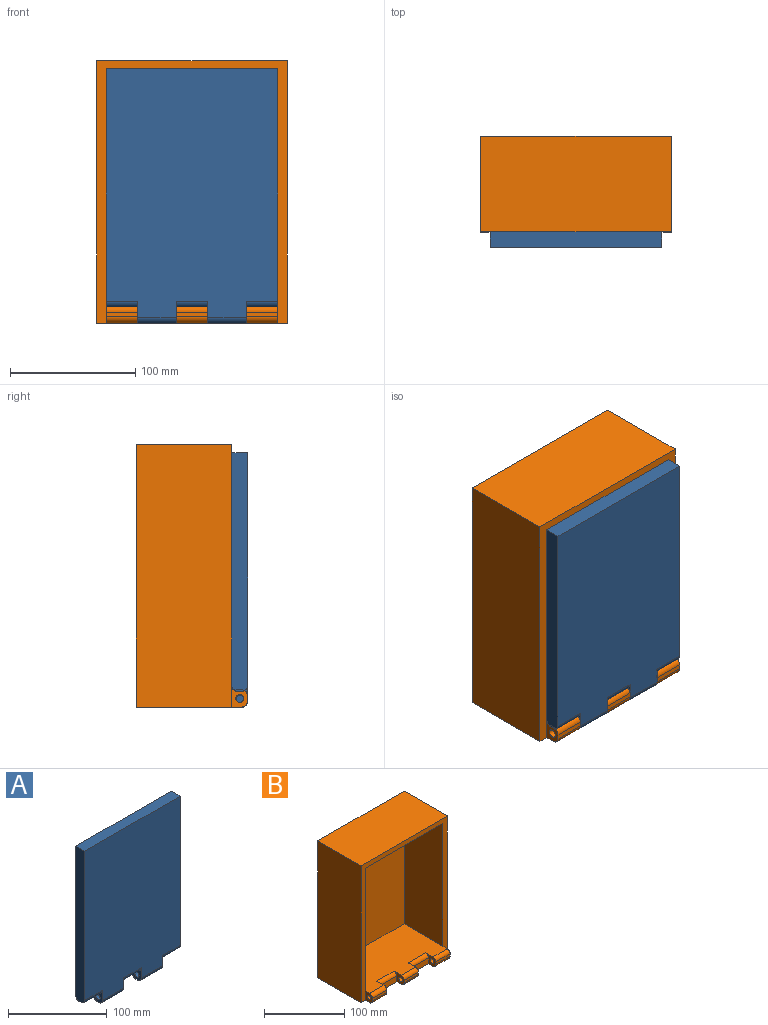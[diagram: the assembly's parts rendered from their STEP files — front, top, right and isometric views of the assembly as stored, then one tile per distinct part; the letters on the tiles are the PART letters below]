
ASSEMBLY  parts=2 mates=1
PART A: 27 faces, bbox 137.2x12.7x203.2 mm
  f0: plane 25.4x2.54mm, normal (0,0,-1), area 64.5mm2, adj f9,f11,f19,f20
  f1: plane 25.4x2.54mm, normal (0,0,-1), area 64.5mm2, adj f3,f8,f25,f26
  f2: plane 137.16x12.7mm, normal (0,0,1), area 1741.9mm2, adj f3,f5,f6,f7
  f3: plane 190.5x12.7mm, normal (-1,0,0), area 2408.3mm2, adj f1,f2,f6,f7,f25,f26
  f4: plane 25.4x2.54mm, normal (0,0,-1), area 64.5mm2, adj f5,f12,f17,f18
  f5: plane 190.5x12.7mm, normal (1,0,0), area 2408.3mm2, adj f2,f4,f6,f7,f17,f18
  f6: plane 198.12x137.16mm, normal (0,-1,0), area 26206.4mm2, adj f2,f3,f5,f8,f9,f11,f12,f17
  f7: plane 198.12x137.16mm, normal (0,1,0), area 26206.4mm2, adj f2,f3,f5,f8,f9,f11,f12,f18
  f8: plane 17.78x12.7mm, normal (-1,0,0), area 129.6mm2, adj f1,f6,f7,f10,f16,f23,f24,f25
  f9: plane 17.78x12.7mm, normal (1,0,0), area 129.6mm2, adj f0,f6,f7,f10,f16,f19,f20,f23
  f10: plane 30.48x2.54mm, normal (0,0,-1), area 77.4mm2, adj f8,f9,f23,f24
  f11: plane 17.78x12.7mm, normal (-1,0,0), area 129.6mm2, adj f0,f6,f7,f13,f15,f19,f20,f21
  f12: plane 17.78x12.7mm, normal (1,0,0), area 161.3mm2, adj f4,f6,f7,f13,f17,f18,f21,f22
  f13: plane 30.48x2.54mm, normal (0,0,-1), area 77.4mm2, adj f11,f12,f21,f22
  f14: plane 6.35x6.35mm, normal (-1,0,0), area 31.7mm2, adj f15
  f15: cylinder r=3.17mm len=20.32mm, axis (-1,0,0), area 405.4mm2, adj f11,f14
  f16: cylinder r=3.17mm len=30.48mm, axis (-1,0,0), area 608mm2, adj f8,f9
  f17: cylinder r=5.08mm len=25.4mm, axis (-1,0,0), area 202.7mm2, adj f4,f5,f6,f12
  f18: cylinder r=5.08mm len=25.4mm, axis (1,0,0), area 202.7mm2, adj f4,f5,f7,f12
  f19: cylinder r=5.08mm len=25.4mm, axis (-1,0,0), area 202.7mm2, adj f0,f6,f9,f11
  f20: cylinder r=5.08mm len=25.4mm, axis (1,0,0), area 202.7mm2, adj f0,f7,f9,f11
  f21: cylinder r=5.08mm len=30.48mm, axis (-1,0,0), area 243.2mm2, adj f7,f11,f12,f13
  f22: cylinder r=5.08mm len=30.48mm, axis (1,0,0), area 243.2mm2, adj f6,f11,f12,f13
  f23: cylinder r=5.08mm len=30.48mm, axis (-1,0,0), area 243.2mm2, adj f7,f8,f9,f10
  f24: cylinder r=5.08mm len=30.48mm, axis (1,0,0), area 243.2mm2, adj f6,f8,f9,f10
  f25: cylinder r=5.08mm len=25.4mm, axis (1,0,0), area 202.7mm2, adj f1,f3,f7,f8
  f26: cylinder r=5.08mm len=25.4mm, axis (-1,0,0), area 202.7mm2, adj f1,f3,f6,f8
PART B: 33 faces, bbox 152.4x88.9x209.6 mm
  f0: plane 30.48x8.89mm, normal (0,-1,0), area 271mm2, adj f16,f18,f21,f32
  f1: plane 30.48x8.89mm, normal (0,-1,0), area 271mm2, adj f13,f19,f21,f31
  f2: plane 209.55x152.4mm, normal (0,-1,0), area 4238.7mm2, adj f3,f4,f5,f7,f9,f10,f12,f15
  f3: plane 209.55x76.2mm, normal (-1,0,0), area 15967.7mm2, adj f2,f5,f6,f21
  f4: plane 209.55x76.2mm, normal (1,0,0), area 15967.7mm2, adj f2,f5,f6,f21
  f5: plane 152.4x76.2mm, normal (0,0,1), area 11612.9mm2, adj f2,f3,f4,f6
  f6: plane 209.55x152.4mm, normal (0,1,0), area 31935.4mm2, adj f3,f4,f5,f21
  f7: plane 187.96x68.58mm, normal (1,0,0), area 12890.3mm2, adj f2,f8,f10,f11
  f8: plane 137.16x76.2mm, normal (0,0,1), area 9677.4mm2, adj f7,f9,f11,f12,f13,f15,f16,f18
  f9: plane 187.96x68.58mm, normal (-1,0,0), area 12890.3mm2, adj f2,f8,f10,f11
  f10: plane 137.16x68.58mm, normal (0,0,-1), area 9406.4mm2, adj f2,f7,f9,f11
  f11: plane 187.96x137.16mm, normal (0,-1,0), area 25780.6mm2, adj f7,f8,f9,f10
  f12: plane 13.97x12.7mm, normal (1,0,0), area 134.7mm2, adj f2,f8,f14,f21,f24,f27,f30
  f13: plane 17.78x13.97mm, normal (-1,0,0), area 140.2mm2, adj f1,f8,f14,f21,f24,f27,f30,f31
  f14: plane 25.4x3.81mm, normal (0,-1,0), area 96.8mm2, adj f12,f13,f27,f30
  f15: plane 13.97x12.7mm, normal (-1,0,0), area 134.7mm2, adj f2,f8,f17,f21,f23,f25,f29
  f16: plane 17.78x13.97mm, normal (1,0,0), area 140.2mm2, adj f0,f8,f17,f21,f23,f25,f29,f32
  f17: plane 25.4x3.81mm, normal (0,-1,0), area 96.8mm2, adj f15,f16,f25,f29
  f18: plane 17.78x13.97mm, normal (-1,0,0), area 140.2mm2, adj f0,f8,f20,f21,f22,f26,f28,f32
  f19: plane 17.78x13.97mm, normal (1,0,0), area 140.2mm2, adj f1,f8,f20,f21,f22,f26,f28,f31
  f20: plane 25.4x3.81mm, normal (0,-1,0), area 96.8mm2, adj f18,f19,f26,f28
  f21: plane 152.4x83.82mm, normal (0,0,-1), area 12193.5mm2, adj f0,f1,f2,f3,f4,f6,f12,f13
  f22: cylinder r=3.17mm len=25.4mm, axis (1,0,0), area 506.7mm2, adj f18,f19
  f23: cylinder r=3.17mm len=25.4mm, axis (1,0,0), area 506.7mm2, adj f15,f16
  f24: cylinder r=3.17mm len=25.4mm, axis (1,0,0), area 506.7mm2, adj f12,f13
  f25: cylinder r=5.08mm len=25.4mm, axis (-1,0,0), area 202.7mm2, adj f15,f16,f17,f21
  f26: cylinder r=5.08mm len=25.4mm, axis (-1,0,0), area 202.7mm2, adj f18,f19,f20,f21
  f27: cylinder r=5.08mm len=25.4mm, axis (-1,0,0), area 202.7mm2, adj f12,f13,f14,f21
  f28: cylinder r=5.08mm len=25.4mm, axis (1,0,0), area 202.7mm2, adj f8,f18,f19,f20
  f29: cylinder r=5.08mm len=25.4mm, axis (1,0,0), area 202.7mm2, adj f8,f15,f16,f17
  f30: cylinder r=5.08mm len=25.4mm, axis (1,0,0), area 202.7mm2, adj f8,f12,f13,f14
  f31: cylinder r=5.08mm len=30.48mm, axis (1,0,0), area 243.2mm2, adj f1,f8,f13,f19
  f32: cylinder r=5.08mm len=30.48mm, axis (1,0,0), area 243.2mm2, adj f0,f8,f16,f18
PLACE A t=(434.56,-73.82,33.88)mm
PLACE B t=(-8.8,2.38,-0.56)mm
MATE revolute A.f12 <-> B.f22  axis (1,0,0) through (64.62,-80.17,-101.52)mm
